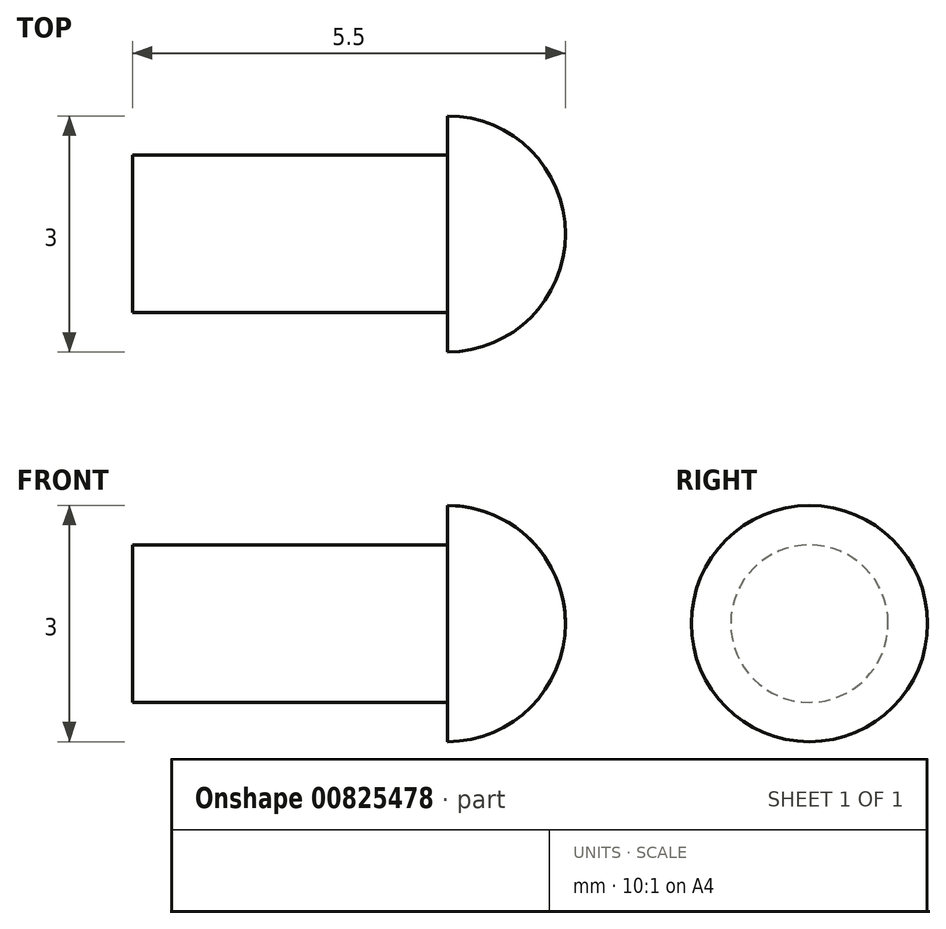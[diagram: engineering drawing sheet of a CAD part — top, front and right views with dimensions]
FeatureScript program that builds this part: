
annotation { "Feature Type Name" : "Feature", "Feature Type Description" : "" }
export const myFeature = defineFeature(function(context is Context, id is Id, definition is map)
    precondition{}
    {
        {
            var Q0;
            Q0=qCreatedBy(makeId("Right.planeOp"),FACE);
            var sketch = newSketch(context, id + "F0", { "sketchPlane" : qUnion([Q0])});
            skCircle(sketch, "E0", {"center": v(0, 0) * mm, "radius": 1 * mm});
            skSolve(sketch);
        }
        {
            var Q0;
            Q0=makeQuery(id+"F0.imprint","IMPRINT",FACE,{"disambiguationData":[TD([[makeQuery(id+"F0.imprint","IMPRINT",EDGE,{"derivedFrom":sQuery(id+"F0.wireOp",EDGE,"E0")}),1.0]])]});
            extrude(context, id + "F1", {"entities" : qUnion([Q0]), "endBound" : BoundingType.SYMMETRIC, "depth" : 4 * mm, "offsetDistance" : 25 * mm});
        }
        {
            var Q0;
            Q0=qCreatedBy(makeId("Front.planeOp"),FACE);
            var sketch = newSketch(context, id + "F2", { "sketchPlane" : qUnion([Q0])});
            skArc(sketch, "E1", {"start": v(3.5, 0) * mm, "mid": v(3.06, 1.06) * mm, "end": v(2, 1.5) * mm});
            skLineSegment(sketch, "E2", {"start": v(2, 0) * mm, "end": v(2, 1.5) * mm});
            skLineSegment(sketch, "E3", {"start": v(2, 0) * mm, "end": v(3.5, 0) * mm});
            skSolve(sketch);
        }
        {
            var Q0;
            Q0=makeQuery(id+"F2.imprint","IMPRINT",FACE,{"disambiguationData":[TD([[makeQuery(id+"F2.imprint","IMPRINT",EDGE,{"derivedFrom":sQuery(id+"F2.wireOp",EDGE,"E1")}),1.0]])]});
            var Q1;
            Q1=makeQuery(id+"F1.opExtrude","CAP_EDGE",EDGE,{"disambiguationData":[OSD([sQuery(id+"F0.wireOp",EDGE,"E0")])],"isStart":false});
            revolve(context, id + "F3", {"operationType" : NewBodyOperationType.ADD, "surfaceOperationType" : NewSurfaceOperationType.NEW, "entities" : qUnion([Q0]), "axis" : qUnion([Q1]), "revolveType" : RevolveType.FULL});
        }
    });
